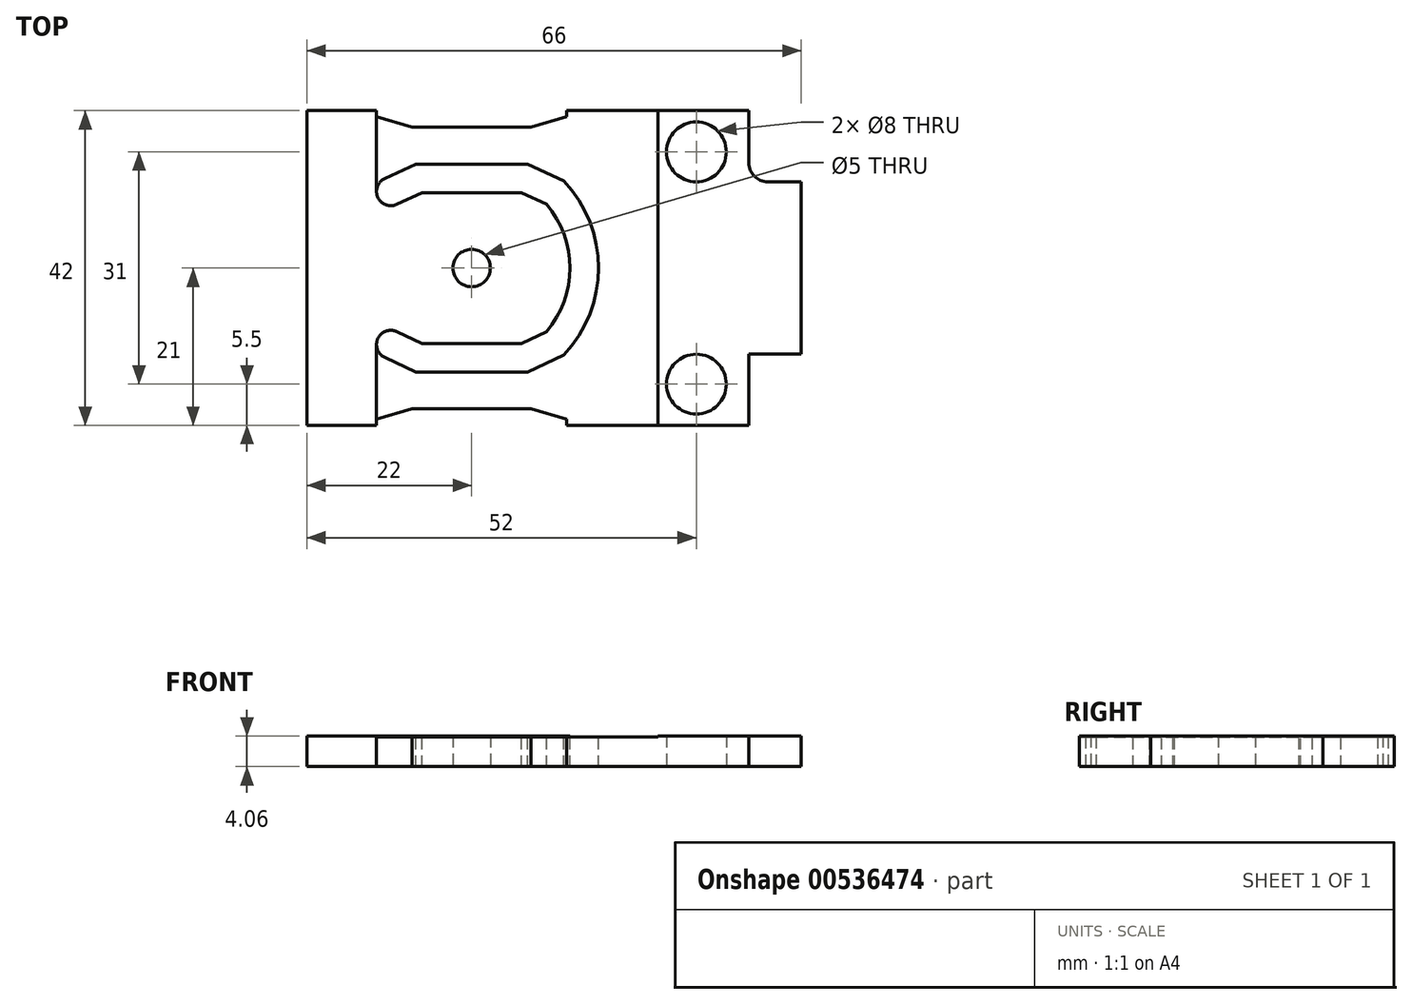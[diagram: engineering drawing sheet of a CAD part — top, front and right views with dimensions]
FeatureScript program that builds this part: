
annotation { "Feature Type Name" : "Feature", "Feature Type Description" : "" }
export const myFeature = defineFeature(function(context is Context, id is Id, definition is map)
    precondition{}
    {
        {
            var Q0;
            Q0=qCreatedBy(makeId("Top.planeOp"),FACE);
            var sketch = newSketch(context, id + "F0", { "sketchPlane" : qUnion([Q0])});
            skLineSegment(sketch, "E0.bottom", {"start": v(-33, 21) * mm, "end": v(33, 21) * mm, "construction": true});
            skLineSegment(sketch, "E0.top", {"start": v(-33, -21) * mm, "end": v(33, -21) * mm, "construction": true});
            skLineSegment(sketch, "E0.left", {"start": v(-33, 21) * mm, "end": v(-33, -21) * mm, "construction": true});
            skLineSegment(sketch, "E0.right", {"start": v(33, 21) * mm, "end": v(33, -21) * mm, "construction": true});
            skLineSegment(sketch, "E1", {"start": v(-33, 21) * mm, "end": v(33, -21) * mm, "construction": true});
            skPoint(sketch, "E2", {"position": v(-11, 0) * mm});
            skPoint(sketch, "E3", {"position": v(19, 15.5) * mm});
            skPoint(sketch, "E4", {"position": v(19, -15.5) * mm});
            skLineSegment(sketch, "E5", {"start": v(19, 15.5) * mm, "end": v(19, -15.5) * mm, "construction": true});
            skLineSegment(sketch, "E6", {"start": v(19, 0) * mm, "end": v(33, 0) * mm, "construction": true});
            skPoint(sketch, "E6.endSnap0", {"position": v(33, 0) * mm});
            skSolve(sketch);
        }
        {
            var Q0;
            Q0=qCreatedBy(makeId("Top.planeOp"),FACE);
            var sketch = newSketch(context, id + "F1", { "sketchPlane" : qUnion([Q0])});
            skLineSegment(sketch, "E7", {"start": v(26, 21) * mm, "end": v(-33, 21) * mm});
            skLineSegment(sketch, "E8", {"start": v(-33, 21) * mm, "end": v(-33, -21) * mm});
            skLineSegment(sketch, "E9", {"start": v(19, 15.5) * mm, "end": v(33, 15.5) * mm, "construction": true});
            skLineSegment(sketch, "E10", {"start": v(26, 15.5) * mm, "end": v(26, 31.74) * mm, "construction": true});
            skLineSegment(sketch, "E11", {"start": v(12, 15.72) * mm, "end": v(12, 31.74) * mm, "construction": true});
            skLineSegment(sketch, "E12", {"start": v(12, 31.74) * mm, "end": v(26, 31.74) * mm, "construction": true});
            skLineSegment(sketch, "E13", {"start": v(19, 15.5) * mm, "end": v(19, 31.74) * mm, "construction": true});
            skCircle(sketch, "E14", {"center": v(19, 15.5) * mm, "radius": 4 * mm});
            skLineSegment(sketch, "E15", {"start": v(26, 21) * mm, "end": v(26, 14.04) * mm});
            skLineSegment(sketch, "E16", {"start": v(28.54, 11.5) * mm, "end": v(33, 11.5) * mm});
            skLineSegment(sketch, "E17", {"start": v(33, 11.5) * mm, "end": v(33, -11.5) * mm});
            skLineSegment(sketch, "E18", {"start": v(33, -11.5) * mm, "end": v(26, -11.5) * mm});
            skLineSegment(sketch, "E19", {"start": v(26, -11.5) * mm, "end": v(26, -21) * mm});
            skLineSegment(sketch, "E20", {"start": v(26, -21) * mm, "end": v(-33, -21) * mm});
            skPoint(sketch, "E21", {"position": v(33, 0) * mm});
            skLineSegment(sketch, "E22", {"start": v(33, 0) * mm, "end": v(7.99, 0) * mm, "construction": true});
            skCircle(sketch, "E23.MirrorC", {"center": v(19, -15.5) * mm, "radius": 4 * mm});
            skPoint(sketch, "E24.visualSharp", {"position": v(26, 11.5) * mm});
            skArc(sketch, "E24.filletArc", {"start": v(26, 14.04) * mm, "mid": v(26.74, 12.24) * mm, "end": v(28.54, 11.5) * mm});
            skSolve(sketch);
        }
        {
            var Q0;
            Q0=makeQuery(id+"F1.imprint","IMPRINT",FACE,{"disambiguationData":[TD([[makeQuery(id+"F1.imprint","IMPRINT",EDGE,{"derivedFrom":sQuery(id+"F1.wireOp",EDGE,"E7")}),1.0]])]});
            var Q1;
            Q1 = qConstructionFilter(qBodyType(qCreatedBy(id + "F1" ,EDGE), BodyType.WIRE), ConstructionObject.NO);
            extrude(context, id + "F2", {"entities" : qUnion([Q0]), "surfaceEntities" : qUnion([Q1]), "depth" : 4.06 * mm, "offsetDistance" : 25.4 * mm});
        }
        {
            var Q0;
            Q0=sQuery(id+"F0.wireOp",VERTEX,"E2");
            var Q1;
            Q1=makeQuery(id+"F2.opExtrude","SWEPT_BODY",BODY,{"disambiguationData":[OSD([sQuery(id+"F1.wireOp",EDGE,"E7"),sQuery(id+"F1.wireOp",EDGE,"E8"),sQuery(id+"F1.wireOp",EDGE,"E14"),sQuery(id+"F1.wireOp",EDGE,"E15"),sQuery(id+"F1.wireOp",EDGE,"E16"),sQuery(id+"F1.wireOp",EDGE,"E17"),sQuery(id+"F1.wireOp",EDGE,"E18"),sQuery(id+"F1.wireOp",EDGE,"E19"),sQuery(id+"F1.wireOp",EDGE,"E20"),sQuery(id+"F1.wireOp",EDGE,"E23.MirrorC"),sQuery(id+"F1.wireOp",EDGE,"E24.filletArc")])]});
            hole(context, id + "F3", {"style" : HoleStyle.SIMPLE, "endStyle" : HoleEndStyle.THROUGH, "oppositeDirection" : true, "standardTappedOrClearance" : lookupTablePath({ "standard" : "ISO", "size" : "5", "type" : "Drilled" }), "standardBlindInLast" : lookupTablePath({ "standard" : "ISO", "size" : "5", "type" : "Drilled" }), "holeDiameter" : 5 * mm, "majorDiameter" : 6.35 * mm, "tappedDepth" : 9.52 * mm, "tapClearance" : 1, "startFromSketch" : true, "locations" : qUnion([Q0]), "scope" : qUnion([Q1])});
        }
        {
            var Q0;
            Q0=makeQuery(id+"F2.opExtrude","CAP_FACE",FACE,{"disambiguationData":[OSD([sQuery(id+"F1.wireOp",EDGE,"E7"),sQuery(id+"F1.wireOp",EDGE,"E8"),sQuery(id+"F1.wireOp",EDGE,"E14"),sQuery(id+"F1.wireOp",EDGE,"E15"),sQuery(id+"F1.wireOp",EDGE,"E16"),sQuery(id+"F1.wireOp",EDGE,"E17"),sQuery(id+"F1.wireOp",EDGE,"E18"),sQuery(id+"F1.wireOp",EDGE,"E19"),sQuery(id+"F1.wireOp",EDGE,"E20"),sQuery(id+"F1.wireOp",EDGE,"E23.MirrorC"),sQuery(id+"F1.wireOp",EDGE,"E24.filletArc")])],"isStart":true});
            var sketch = newSketch(context, id + "F4", { "sketchPlane" : qUnion([Q0])});
            skLineSegment(sketch, "E25", {"start": v(-23.7, -21) * mm, "end": v(-23.7, -20.2) * mm});
            skLineSegment(sketch, "E26", {"start": v(-23.7, -20.2) * mm, "end": v(-18.94, -18.78) * mm});
            skLineSegment(sketch, "E27", {"start": v(-18.94, -18.78) * mm, "end": v(-3.06, -18.78) * mm});
            skLineSegment(sketch, "E28", {"start": v(-3.06, -18.78) * mm, "end": v(1.7, -20.2) * mm});
            skLineSegment(sketch, "E29", {"start": v(1.7, -20.2) * mm, "end": v(1.7, -21) * mm});
            skLineSegment(sketch, "E30", {"start": v(1.7, -21) * mm, "end": v(-23.7, -21) * mm});
            skLineSegment(sketch, "E31", {"start": v(-11, 0) * mm, "end": v(-11, -18.78) * mm, "construction": true});
            skLineSegment(sketch, "E32", {"start": v(-11, 0) * mm, "end": v(48.35, 0) * mm, "construction": true});
            skLineSegment(sketch, "E33.MirrorCS", {"start": v(-23.7, 21) * mm, "end": v(-23.7, 20.2) * mm});
            skLineSegment(sketch, "E34.MirrorCS", {"start": v(1.7, 20.2) * mm, "end": v(1.7, 21) * mm});
            skLineSegment(sketch, "E35.MirrorCS", {"start": v(-23.7, 20.2) * mm, "end": v(-18.94, 18.78) * mm});
            skLineSegment(sketch, "E36.MirrorCS", {"start": v(-3.06, 18.78) * mm, "end": v(1.7, 20.2) * mm});
            skLineSegment(sketch, "E37.MirrorCS", {"start": v(1.7, 21) * mm, "end": v(-23.7, 21) * mm});
            skLineSegment(sketch, "E38.MirrorCS", {"start": v(-18.94, 18.78) * mm, "end": v(-3.06, 18.78) * mm});
            skSolve(sketch);
        }
        {
            var Q0;
            Q0 = qSketchRegion(id + "F4", true);
            extrude(context, id + "F5", {"entities" : qUnion([Q0]), "operationType" : NewBodyOperationType.REMOVE, "oppositeDirection" : true, "depth" : 25.4 * mm, "offsetDistance" : 25.4 * mm});
        }
        {
            var Q0;
            Q0=makeQuery(id+"F2.opExtrude","CAP_FACE",FACE,{"disambiguationData":[OSD([sQuery(id+"F1.wireOp",EDGE,"E7"),sQuery(id+"F1.wireOp",EDGE,"E8"),sQuery(id+"F1.wireOp",EDGE,"E14"),sQuery(id+"F1.wireOp",EDGE,"E15"),sQuery(id+"F1.wireOp",EDGE,"E16"),sQuery(id+"F1.wireOp",EDGE,"E17"),sQuery(id+"F1.wireOp",EDGE,"E18"),sQuery(id+"F1.wireOp",EDGE,"E19"),sQuery(id+"F1.wireOp",EDGE,"E20"),sQuery(id+"F1.wireOp",EDGE,"E23.MirrorC"),sQuery(id+"F1.wireOp",EDGE,"E24.filletArc")])],"isStart":false});
            var sketch = newSketch(context, id + "F6", { "sketchPlane" : qUnion([Q0])});
            skLineSegment(sketch, "E39", {"start": v(-20.99, 8.5) * mm, "end": v(-17.62, 10.07) * mm});
            skLineSegment(sketch, "E40", {"start": v(-17.62, 10.07) * mm, "end": v(-4.38, 10.07) * mm});
            skLineSegment(sketch, "E41", {"start": v(-4.38, 10.07) * mm, "end": v(-1.01, 8.5) * mm});
            skArc(sketch, "E42", {"start": v(2.12, 0) * mm, "mid": v(1.3, 4.53) * mm, "end": v(-1.01, 8.5) * mm});
            skLineSegment(sketch, "E43", {"start": v(-11, 0) * mm, "end": v(-11, 10.07) * mm, "construction": true});
            skArc(sketch, "E44.0", {"start": v(5.93, 0) * mm, "mid": v(4.73, 6.25) * mm, "end": v(1.3, 11.62) * mm});
            skLineSegment(sketch, "E44.1", {"start": v(-3.53, 13.88) * mm, "end": v(1.3, 11.62) * mm});
            skLineSegment(sketch, "E44.2", {"start": v(-18.47, 13.88) * mm, "end": v(-3.53, 13.88) * mm});
            skLineSegment(sketch, "E44.3", {"start": v(-22.6, 11.95) * mm, "end": v(-18.47, 13.88) * mm});
            skLineSegment(sketch, "E45.0", {"start": v(32.35, 17.85) * mm, "end": v(32.35, 27.35) * mm});
            skLineSegment(sketch, "E45.1", {"start": v(39.35, 17.85) * mm, "end": v(32.35, 17.85) * mm});
            skLineSegment(sketch, "E45.2", {"start": v(39.35, -17.85) * mm, "end": v(39.35, 17.85) * mm});
            skLineSegment(sketch, "E45.3", {"start": v(32.35, -17.85) * mm, "end": v(39.35, -17.85) * mm});
            skLineSegment(sketch, "E45.4", {"start": v(32.35, -27.35) * mm, "end": v(32.35, -17.85) * mm});
            skLineSegment(sketch, "E45.5", {"start": v(-17.35, 27.35) * mm, "end": v(-39.35, 27.35) * mm});
            skLineSegment(sketch, "E45.6", {"start": v(-17.35, 25.13) * mm, "end": v(-17.35, 27.35) * mm});
            skLineSegment(sketch, "E45.7", {"start": v(-4.65, 25.13) * mm, "end": v(-17.35, 25.13) * mm});
            skLineSegment(sketch, "E45.8", {"start": v(-4.65, 27.35) * mm, "end": v(-4.65, 25.13) * mm});
            skLineSegment(sketch, "E45.9", {"start": v(-39.35, 27.35) * mm, "end": v(-39.35, -27.35) * mm});
            skLineSegment(sketch, "E45.10", {"start": v(-39.35, -27.35) * mm, "end": v(-17.35, -27.35) * mm});
            skLineSegment(sketch, "E45.11", {"start": v(-17.35, -27.35) * mm, "end": v(-17.35, -25.13) * mm});
            skLineSegment(sketch, "E45.12", {"start": v(-17.35, -25.13) * mm, "end": v(-4.65, -25.13) * mm});
            skLineSegment(sketch, "E45.13", {"start": v(-4.65, -25.13) * mm, "end": v(-4.65, -27.35) * mm});
            skLineSegment(sketch, "E45.14", {"start": v(32.35, 27.35) * mm, "end": v(-4.65, 27.35) * mm});
            skLineSegment(sketch, "E45.15", {"start": v(-4.65, -27.35) * mm, "end": v(32.35, -27.35) * mm});
            skLineSegment(sketch, "E46", {"start": v(-11, 0) * mm, "end": v(4.8, 0) * mm, "construction": true});
            skLineSegment(sketch, "E47", {"start": v(-20.99, 8.5) * mm, "end": v(-22.6, 11.95) * mm, "construction": true});
            skArc(sketch, "E48", {"start": v(-22.6, 11.95) * mm, "mid": v(-23.52, 9.42) * mm, "end": v(-20.99, 8.5) * mm});
            skLineSegment(sketch, "E49.MirrorCS", {"start": v(-4.38, -10.07) * mm, "end": v(-1.01, -8.5) * mm});
            skArc(sketch, "E50.MirrorCS", {"start": v(-22.6, -11.95) * mm, "mid": v(-23.52, -9.42) * mm, "end": v(-20.99, -8.5) * mm});
            skLineSegment(sketch, "E51.MirrorCS", {"start": v(-20.99, -8.5) * mm, "end": v(-22.6, -11.95) * mm, "construction": true});
            skLineSegment(sketch, "E52.MirrorCS", {"start": v(-17.62, -10.07) * mm, "end": v(-4.38, -10.07) * mm});
            skArc(sketch, "E53.MirrorCS", {"start": v(5.93, 0) * mm, "mid": v(4.73, -6.25) * mm, "end": v(1.3, -11.62) * mm});
            skArc(sketch, "E54.MirrorCS", {"start": v(2.12, 0) * mm, "mid": v(1.3, -4.53) * mm, "end": v(-1.01, -8.5) * mm});
            skLineSegment(sketch, "E55.MirrorCS", {"start": v(-3.53, -13.88) * mm, "end": v(1.3, -11.62) * mm});
            skLineSegment(sketch, "E56.MirrorCS", {"start": v(-11, 0) * mm, "end": v(-11, -10.07) * mm, "construction": true});
            skLineSegment(sketch, "E57.MirrorCS", {"start": v(-20.99, -8.5) * mm, "end": v(-17.62, -10.07) * mm});
            skLineSegment(sketch, "E58.MirrorCS", {"start": v(-22.6, -11.95) * mm, "end": v(-18.47, -13.88) * mm});
            skLineSegment(sketch, "E59.MirrorCS", {"start": v(-18.47, -13.88) * mm, "end": v(-3.53, -13.88) * mm});
            skLineSegment(sketch, "E60", {"start": v(-23.7, 20.2) * mm, "end": v(-23.7, -20.2) * mm, "construction": true});
            skSolve(sketch);
        }
        {
            var Q0;
            Q0=makeQuery(id+"F6.imprint","IMPRINT",FACE,{"disambiguationData":[TD([[makeQuery(id+"F6.imprint","IMPRINT",EDGE,{"derivedFrom":sQuery(id+"F6.wireOp",EDGE,"E39")}),1.0]])]});
            extrude(context, id + "F7", {"entities" : qUnion([Q0]), "operationType" : NewBodyOperationType.REMOVE, "oppositeDirection" : true, "depth" : 25.4 * mm, "offsetDistance" : 25.4 * mm});
        }
        {
            var Q0;
            Q0=makeQuery(id+"F2.opExtrude","CAP_FACE",FACE,{"disambiguationData":[OSD([sQuery(id+"F1.wireOp",EDGE,"E7"),sQuery(id+"F1.wireOp",EDGE,"E8"),sQuery(id+"F1.wireOp",EDGE,"E14"),sQuery(id+"F1.wireOp",EDGE,"E15"),sQuery(id+"F1.wireOp",EDGE,"E16"),sQuery(id+"F1.wireOp",EDGE,"E17"),sQuery(id+"F1.wireOp",EDGE,"E18"),sQuery(id+"F1.wireOp",EDGE,"E19"),sQuery(id+"F1.wireOp",EDGE,"E20"),sQuery(id+"F1.wireOp",EDGE,"E23.MirrorC"),sQuery(id+"F1.wireOp",EDGE,"E24.filletArc")])],"isStart":false});
            var sketch = newSketch(context, id + "F8", { "sketchPlane" : qUnion([Q0])});
            skLineSegment(sketch, "E61.bottom", {"start": v(-23.7, 21) * mm, "end": v(13.85, 21) * mm});
            skLineSegment(sketch, "E61.top", {"start": v(-23.7, 10.07) * mm, "end": v(2.12, 10.07) * mm});
            skLineSegment(sketch, "E61.left", {"start": v(-23.7, 21) * mm, "end": v(-23.7, 10.07) * mm});
            skLineSegment(sketch, "E62.right", {"start": v(13.85, 21) * mm, "end": v(13.85, 0) * mm});
            skLineSegment(sketch, "E63", {"start": v(-11, 0) * mm, "end": v(-4.43, 0) * mm, "construction": true});
            skLineSegment(sketch, "E64.MirrorCS", {"start": v(-23.7, -21) * mm, "end": v(-23.7, -10.07) * mm});
            skLineSegment(sketch, "E65.MirrorCS", {"start": v(-23.7, -10.07) * mm, "end": v(2.12, -10.07) * mm});
            skLineSegment(sketch, "E66.MirrorCS", {"start": v(-23.7, -21) * mm, "end": v(13.85, -21) * mm});
            skLineSegment(sketch, "E67.MirrorCS", {"start": v(13.85, -21) * mm, "end": v(13.85, 0) * mm});
            skLineSegment(sketch, "E68", {"start": v(2.12, 10.07) * mm, "end": v(2.12, -10.07) * mm});
            skSolve(sketch);
        }
        {
            var Q0;
            Q0 = qSketchRegion(id + "F8", true);
            extrude(context, id + "F9", {"entities" : qUnion([Q0]), "operationType" : NewBodyOperationType.REMOVE, "oppositeDirection" : true, "depth" : 0.13 * mm, "offsetDistance" : 25.4 * mm});
        }
    });
